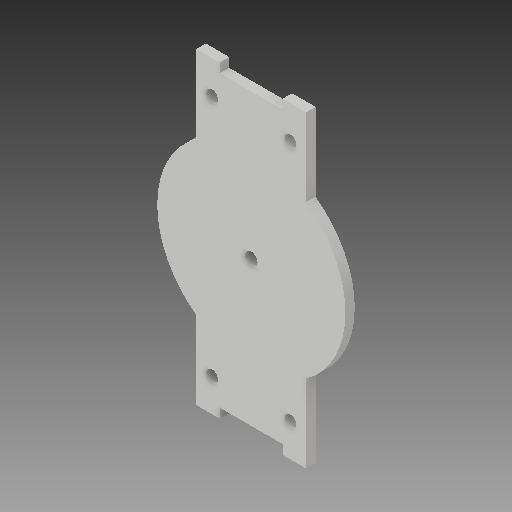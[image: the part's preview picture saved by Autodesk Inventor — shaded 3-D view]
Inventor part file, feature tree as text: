
AUTODESK INVENTOR PART (.ipt)
format: ipt  version: 2018 (Build 220112000, 112)  size: 142,848 bytes
history: native  units: in
note: dims shown in document units (in); Inventor stores cm internally (conversion verified against a paired STEP export)
features: reference x10, other x7, extrude x3, sketch x3
ambient origin geometry x8: Origin, YZ Plane, XZ Plane, XY Plane, X Axis, Y Axis, Z Axis, Center Point
bodies: Solid1 (feature_tree)
feature tree (23):
  extrude  "Extrusion1"  Depth=1.378in
  extrude  "Extrusion2"  Depth=0.1181in TaperAngle=0.0deg
  extrude  "Extrusion3"  Depth=0.1575in
  sketch  "Sketch1"  dims[d0=2.3622in d1=1.378in]
  reference  "Reference1"
  reference  "Reference2"
  reference  "Reference3"
  reference  "Reference4"
  reference  "Reference5"
  reference  "Reference6"
  sketch  "Sketch2"  dims[d2=1.378in d3=0.1181in d4=0.0in]
  reference  "Reference7"
  reference  "Reference8"
  reference  "Reference9"
  reference  "Reference10"
  sketch  "Sketch3"  dims[d5=1.0694in d6=0.0in d7=0.1575in d8=0.5694in d9=0.0in]
  other  "Camera pan and tilt assembly.iam"
  other  "Camera mount raiser:3"
  other  "Camera mount raiser:2"
  other  "Angle bracket long:1"
  other  "Angle bracket long:2"
  other  "Angle bracket long:3"
  other  "Angle bracket long:4"
